# Revit family: Lixil-Grohe-Listra-Towel_Ring-106260_0
name_source: partatom
category: Specialty Equipment
units: mm (PartAtom-declared; Revit-internal decimal feet)

## family parameters
Cut with Voids When Loaded = No
Enable Cutting in Views = Yes
Host = Face
Maintain Annotation Orientation = No
OmniClass Number = 23.45.55.17
OmniClass Title = Mixing Faucets
Part Type = Normal
Room Calculation Point = No
Round Connector Dimension = Use Diameter
Shared = No

## types (1)
- Listra Towel Ring
    Assembly Code = D2010400
    Brand = Grohe
    Collection = Listra
    Default Elevation = 0"
    Depth = 2 11/16"
    Description = Towel Ring
    Finish = Metal - Grohe - Chrome
    Height = 5 3/4"
    Keynote = 22 40 00
    Manufacturer = LIXIL
    Model = 106260_0
    Product Documentation Link = https://www.grohe.us
    Product Name = Listra Towel Ring
    Product Page URL = https://www.grohe.us
    URL = https://www.grohe.us
    Version = 2023 - v1.0a
    Warranty URL = https://www.grohe.us
    Width = 8 3/8"

## geometry (parser evidence)
native form markers: Sweep x2
no freeform markers — native parametric forms only
